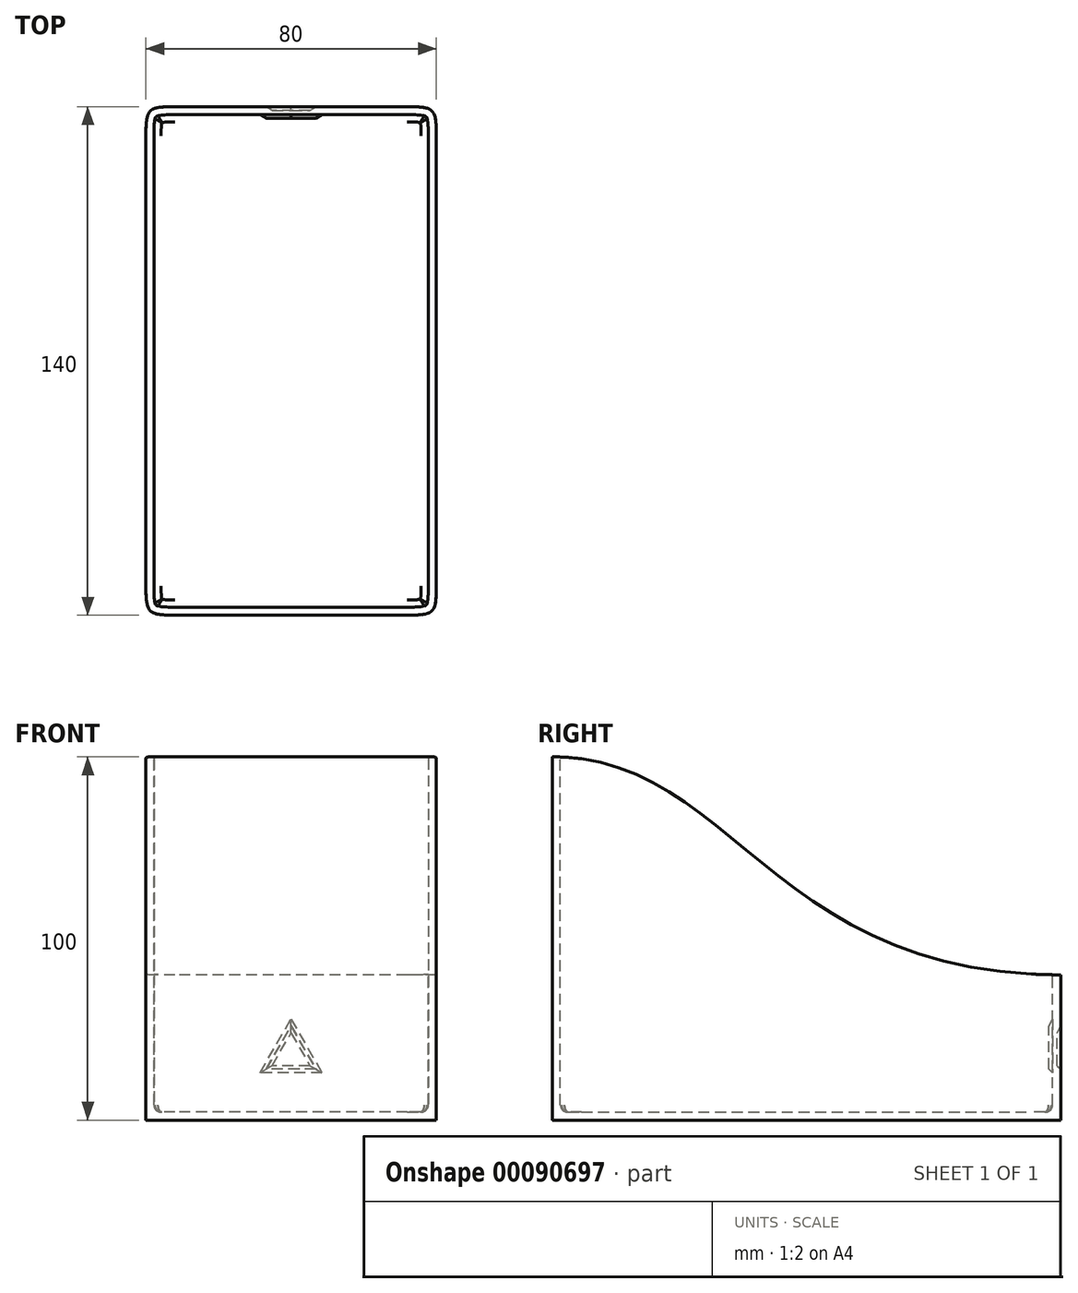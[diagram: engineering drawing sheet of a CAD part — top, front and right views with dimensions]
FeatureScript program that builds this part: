
annotation { "Feature Type Name" : "Feature", "Feature Type Description" : "" }
export const myFeature = defineFeature(function(context is Context, id is Id, definition is map)
    precondition{}
    {
        {
            var Q0;
            Q0=qCreatedBy(makeId("Right.planeOp"),FACE);
            var sketch = newSketch(context, id + "F0", { "sketchPlane" : qUnion([Q0])});
            skLineSegment(sketch, "E0", {"start": v(0, 0) * mm, "end": v(140, 0) * mm});
            skLineSegment(sketch, "E1", {"start": v(140, 0) * mm, "end": v(140, 40) * mm});
            skLineSegment(sketch, "E2", {"start": v(0, 100) * mm, "end": v(0, 0) * mm});
            skFitSpline(sketch, "E3", {"points": [v(0, 100) * mm, v(140, 40) * mm], "startDerivative": vector(150, 0) * mm, "endDerivative": vector(240, 0) * mm});
            skLineSegment(sketch, "E4", {"start": v(50, 100) * mm, "end": v(60, 40) * mm, "construction": true});
            skSolve(sketch);
        }
        {
            var Q0;
            Q0=makeQuery(id+"F0.imprint","IMPRINT",FACE,{"disambiguationData":[TD([[makeQuery(id+"F0.imprint","IMPRINT",EDGE,{"derivedFrom":sQuery(id+"F0.wireOp",EDGE,"E0")}),1.0]])]});
            extrude(context, id + "F1", {"entities" : qUnion([Q0]), "endBound" : BoundingType.SYMMETRIC, "depth" : 80 * mm});
        }
        {
            var Q0;
            Q0=makeQuery(id+"F1.opExtrude","CAP_EDGE",EDGE,{"disambiguationData":[OSD([sQuery(id+"F0.wireOp",EDGE,"E2")])],"isStart":false});
            var Q1;
            Q1=makeQuery(id+"F1.opExtrude","CAP_EDGE",EDGE,{"disambiguationData":[OSD([sQuery(id+"F0.wireOp",EDGE,"E1")])],"isStart":false});
            var Q2;
            Q2=makeQuery(id+"F1.opExtrude","CAP_EDGE",EDGE,{"disambiguationData":[OSD([sQuery(id+"F0.wireOp",EDGE,"E1")])],"isStart":true});
            var Q3;
            Q3=makeQuery(id+"F1.opExtrude","CAP_EDGE",EDGE,{"disambiguationData":[OSD([sQuery(id+"F0.wireOp",EDGE,"E2")])],"isStart":true});
            fillet(context, id + "F2", {"entities" : qUnion([Q0, Q1, Q2, Q3]), "radius" : 8 * mm, "tangentPropagation" : true, "rho" : .7, "crossSection" : FilletCrossSection.CONIC, "allowEdgeOverflow" : false});
        }
        {
            var Q0;
            Q0=makeQuery(id+"F1.opExtrude","SWEPT_FACE",FACE,{"disambiguationData":[OSD([sQuery(id+"F0.wireOp",EDGE,"E1")])]});
            var sketch = newSketch(context, id + "F3", { "sketchPlane" : qUnion([Q0])});
            skLineSegment(sketch, "E5", {"start": v(0, 26) * mm, "end": v(-6.93, 14) * mm});
            skLineSegment(sketch, "E6", {"start": v(-6.93, 14) * mm, "end": v(6.93, 14) * mm});
            skLineSegment(sketch, "E7", {"start": v(6.93, 14) * mm, "end": v(0, 26) * mm});
            skLineSegment(sketch, "E8", {"start": v(0, 26) * mm, "end": v(0, 40) * mm, "construction": true});
            skLineSegment(sketch, "E9", {"start": v(0, 14) * mm, "end": v(0, 0) * mm, "construction": true});
            skSolve(sketch);
        }
        {
            var Q0;
            Q0=makeQuery(id+"F3.imprint","IMPRINT",FACE,{"disambiguationData":[TD([[makeQuery(id+"F3.imprint","IMPRINT",EDGE,{"derivedFrom":sQuery(id+"F3.wireOp",EDGE,"E5")}),1.0]])]});
            extrude(context, id + "F4", {"entities" : qUnion([Q0]), "operationType" : NewBodyOperationType.REMOVE, "oppositeDirection" : true, "depth" : 1 * mm, "hasDraft" : true, "draftAngle" : 45 * degree, "draftPullDirection" : true});
        }
        {
            var Q0;
            Q0=makeQuery(id+"F1.opExtrude","SWEPT_FACE",FACE,{"disambiguationData":[OSD([sQuery(id+"F0.wireOp",EDGE,"E3")])]});
            shell(context, id + "F5", {"entities" : qUnion([Q0]), "thickness" : 2.2 * mm});
        }
        {
            var Q0;
            Q0=makeQuery(id+"F5.opShell","OFFSET_FACE",FACE,{"disambiguationData":[OSD([sQuery(id+"F0.wireOp",EDGE,"E0")])]});
            fillet(context, id + "F6", {"entities" : qUnion([Q0]), "radius" : 2 * mm, "tangentPropagation" : true, "allowEdgeOverflow" : false});
        }
    });
